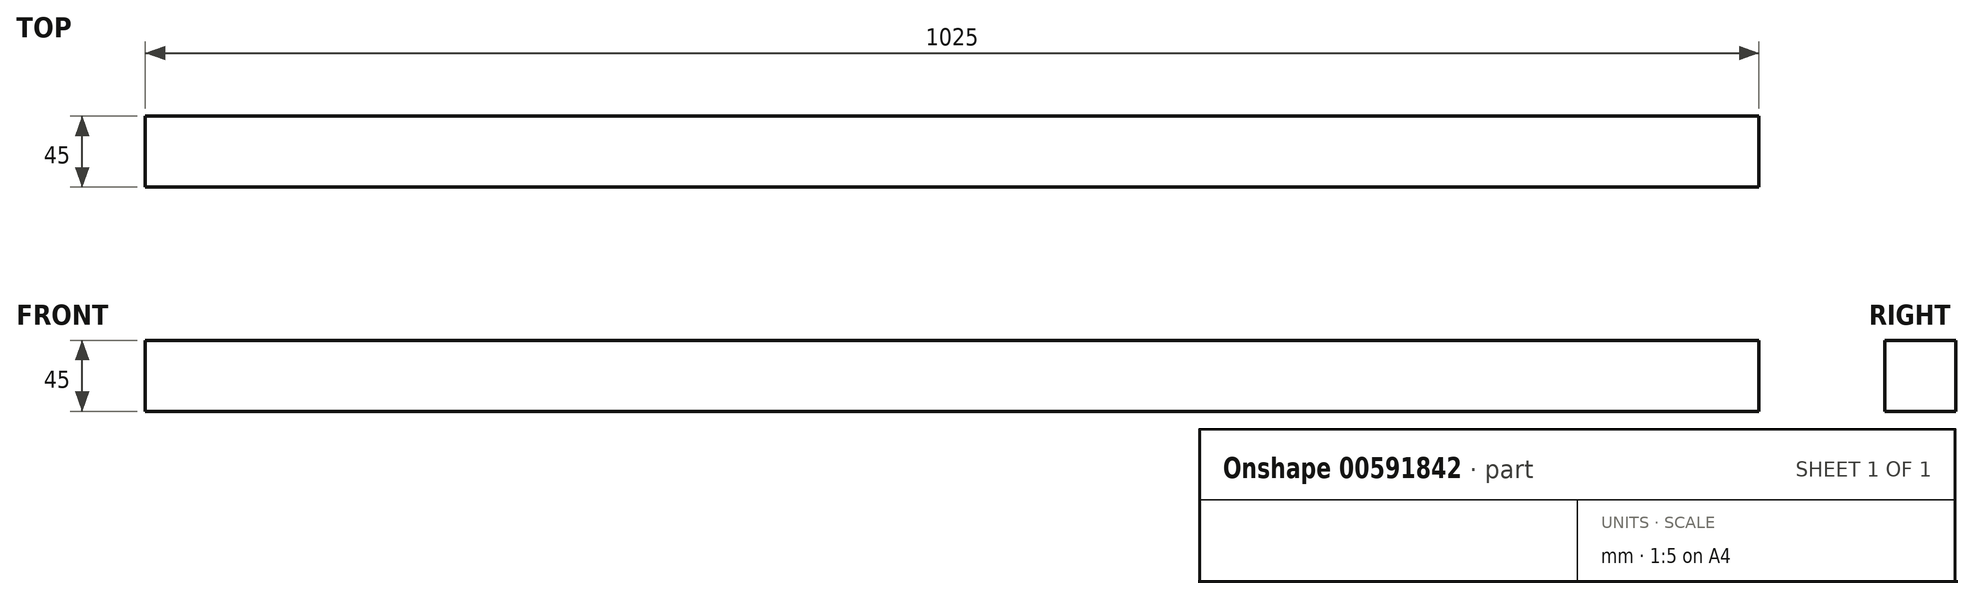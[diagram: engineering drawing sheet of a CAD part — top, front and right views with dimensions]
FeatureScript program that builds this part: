
annotation { "Feature Type Name" : "Feature", "Feature Type Description" : "" }
export const myFeature = defineFeature(function(context is Context, id is Id, definition is map)
    precondition{}
    {
        {
            var Q0;
            Q0=qCreatedBy(makeId("Right.planeOp"),FACE);
            var sketch = newSketch(context, id + "F0", { "sketchPlane" : qUnion([Q0])});
            skLineSegment(sketch, "E0.bottom", {"start": v(0, 0) * mm, "end": v(45, 0) * mm});
            skLineSegment(sketch, "E0.top", {"start": v(0, 45) * mm, "end": v(45, 45) * mm});
            skLineSegment(sketch, "E0.left", {"start": v(0, 0) * mm, "end": v(0, 45) * mm});
            skLineSegment(sketch, "E0.right", {"start": v(45, 0) * mm, "end": v(45, 45) * mm});
            skSolve(sketch);
        }
        {
            var Q0;
            Q0=makeQuery(id+"F0.imprint","IMPRINT",FACE,{"disambiguationData":[TD([[makeQuery(id+"F0.imprint","IMPRINT",EDGE,{"derivedFrom":sQuery(id+"F0.wireOp",EDGE,"E0.bottom")}),1.0]])]});
            extrude(context, id + "F1", {"entities" : qUnion([Q0]), "depth" : 1025 * mm, "offsetDistance" : 25 * mm});
        }
    });
